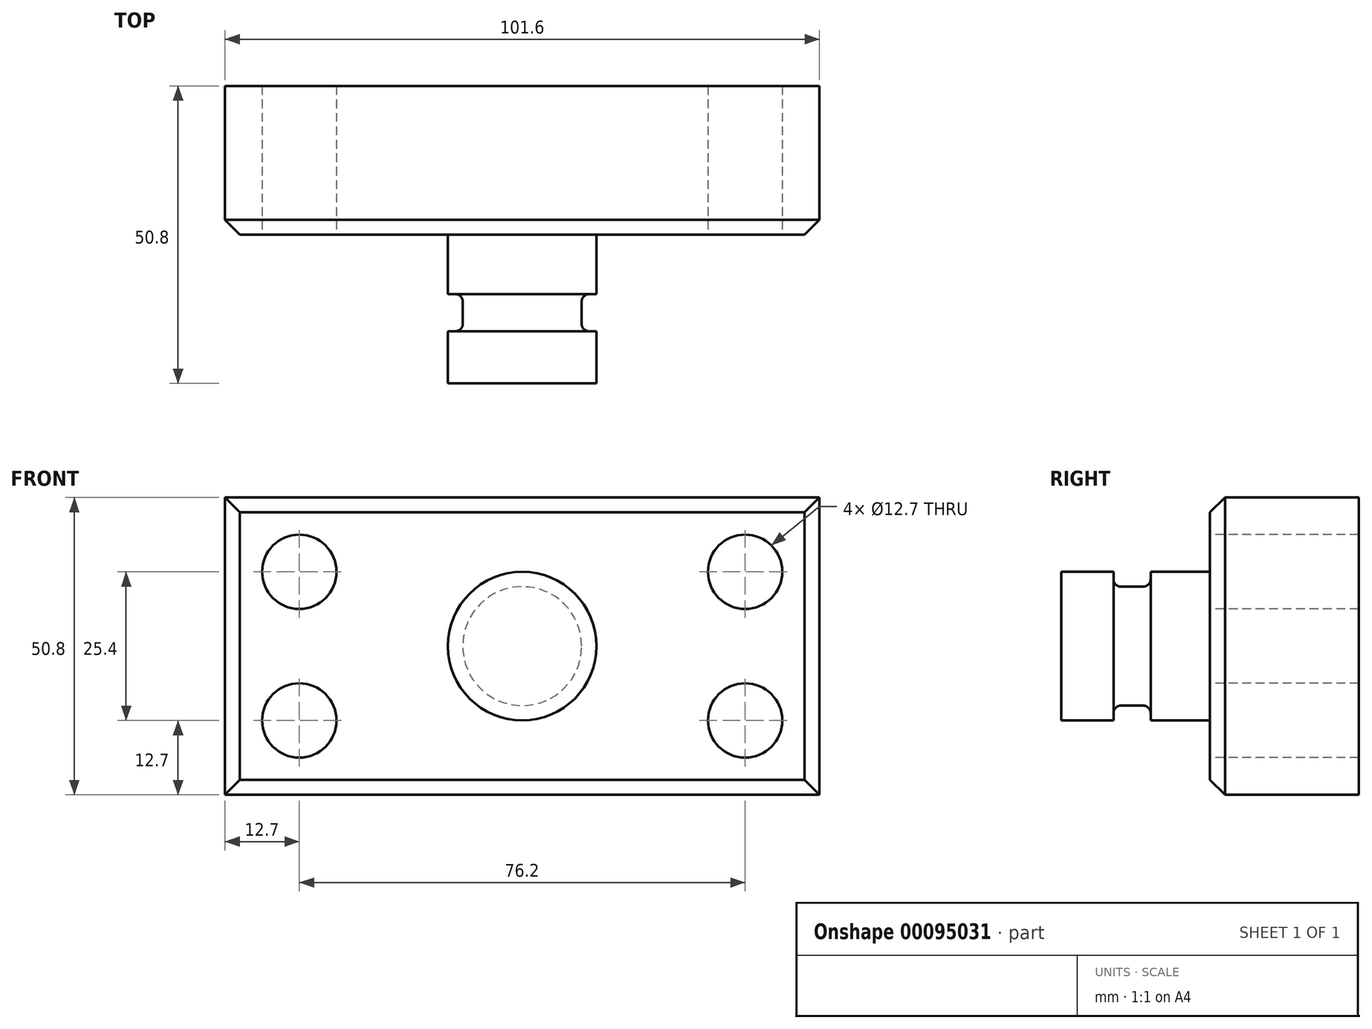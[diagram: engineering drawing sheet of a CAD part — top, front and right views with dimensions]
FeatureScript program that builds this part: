
annotation { "Feature Type Name" : "Feature", "Feature Type Description" : "" }
export const myFeature = defineFeature(function(context is Context, id is Id, definition is map)
    precondition{}
    {
        {
            var Q0;
            Q0=qCreatedBy(makeId("Front.planeOp"),FACE);
            var sketch = newSketch(context, id + "F0", { "sketchPlane" : qUnion([Q0])});
            skLineSegment(sketch, "E0.bottom", {"start": v(-50.8, 25.4) * mm, "end": v(50.8, 25.4) * mm});
            skLineSegment(sketch, "E0.top", {"start": v(-50.8, -25.4) * mm, "end": v(50.8, -25.4) * mm});
            skLineSegment(sketch, "E0.left", {"start": v(-50.8, 25.4) * mm, "end": v(-50.8, -25.4) * mm});
            skLineSegment(sketch, "E0.right", {"start": v(50.8, 25.4) * mm, "end": v(50.8, -25.4) * mm});
            skPoint(sketch, "E0.middle", {"position": v(0, 0) * mm});
            skSolve(sketch);
        }
        {
            var Q0;
            Q0 = qSketchRegion(id + "F0", true);
            extrude(context, id + "F1", {"entities" : qUnion([Q0]), "depth" : 25.4 * mm});
        }
        {
            var Q0;
            Q0=makeQuery(id+"F1.opExtrude","CAP_FACE",FACE,{"disambiguationData":[OSD([sQuery(id+"F0.wireOp",EDGE,"E0.bottom"),sQuery(id+"F0.wireOp",EDGE,"E0.top"),sQuery(id+"F0.wireOp",EDGE,"E0.left"),sQuery(id+"F0.wireOp",EDGE,"E0.right")])],"isStart":false});
            var sketch = newSketch(context, id + "F2", { "sketchPlane" : qUnion([Q0])});
            skCircle(sketch, "E1", {"center": v(-38.1, 12.7) * mm, "radius": 6.35 * mm});
            skCircle(sketch, "E2", {"center": v(-38.1, -12.7) * mm, "radius": 6.35 * mm});
            skCircle(sketch, "E3", {"center": v(38.1, 12.7) * mm, "radius": 6.35 * mm});
            skCircle(sketch, "E4", {"center": v(38.1, -12.7) * mm, "radius": 6.35 * mm});
            skSolve(sketch);
        }
        {
            var Q0;
            Q0 = qSketchRegion(id + "F2", true);
            extrude(context, id + "F3", {"entities" : qUnion([Q0]), "operationType" : NewBodyOperationType.REMOVE, "endBound" : BoundingType.THROUGH_ALL, "oppositeDirection" : true, "depth" : 25.4 * mm});
        }
        {
            var Q0;
            Q0=qCreatedBy(makeId("Top.planeOp"),FACE);
            var sketch = newSketch(context, id + "F4", { "sketchPlane" : qUnion([Q0])});
            skLineSegment(sketch, "E5.bottom", {"start": v(0, -25.4) * mm, "end": v(-12.7, -25.4) * mm});
            skLineSegment(sketch, "E5.top", {"start": v(0, -50.8) * mm, "end": v(-12.7, -50.8) * mm});
            skLineSegment(sketch, "E5.left", {"start": v(0, -25.4) * mm, "end": v(0, -50.8) * mm});
            skLineSegment(sketch, "E5.right", {"start": v(-12.7, -25.4) * mm, "end": v(-12.7, -50.8) * mm});
            skSolve(sketch);
        }
        {
            var Q0;
            Q0 = qSketchRegion(id + "F4", true);
            var Q1;
            Q1=sQuery(id+"F4.wireOp",EDGE,"E5.left");
            revolve(context, id + "F5", {"operationType" : NewBodyOperationType.ADD, "entities" : qUnion([Q0]), "axis" : qUnion([Q1]), "revolveType" : RevolveType.FULL});
        }
        {
            var Q0;
            Q0=qCreatedBy(makeId("Top.planeOp"),FACE);
            var sketch = newSketch(context, id + "F6", { "sketchPlane" : qUnion([Q0])});
            skLineSegment(sketch, "E6.bottom", {"start": v(-14.4, -41.91) * mm, "end": v(-10.16, -41.91) * mm});
            skLineSegment(sketch, "E6.top", {"start": v(-14.4, -35.56) * mm, "end": v(-10.16, -35.56) * mm});
            skLineSegment(sketch, "E6.left", {"start": v(-14.4, -41.91) * mm, "end": v(-14.4, -35.56) * mm});
            skLineSegment(sketch, "E6.right", {"start": v(-10.16, -41.91) * mm, "end": v(-10.16, -35.56) * mm});
            skLineSegment(sketch, "E7", {"start": v(0, 0) * mm, "end": v(0, -61.96) * mm, "construction": true});
            skSolve(sketch);
        }
        {
            var Q0;
            Q0 = qSketchRegion(id + "F6", true);
            var Q1;
            Q1=sQuery(id+"F6.wireOp",EDGE,"E7");
            revolve(context, id + "F7", {"operationType" : NewBodyOperationType.REMOVE, "entities" : qUnion([Q0]), "axis" : qUnion([Q1]), "revolveType" : RevolveType.FULL, "oppositeDirection" : true});
        }
        {
            var Q0;
            Q0=makeQuery(id+"F5.opRevolve","SWEPT_EDGE",EDGE,{"disambiguationData":[OSD([sQuery(id+"F4.wireOp",EDGE,"E5.bottom"),sQuery(id+"F4.wireOp",EDGE,"E5.right")])]});
            var Q1;
            Q1=makeQuery(id+"F7.boolean.opBoolean","COPY",EDGE,{"derivedFrom":makeQuery(id+"F7.opRevolve","SWEPT_EDGE",EDGE,{"disambiguationData":[OSD([sQuery(id+"F6.wireOp",EDGE,"E6.bottom"),sQuery(id+"F6.wireOp",EDGE,"E6.right")])]})});
            var Q2;
            Q2=makeQuery(id+"F7.boolean.opBoolean","COPY",EDGE,{"derivedFrom":makeQuery(id+"F7.opRevolve","SWEPT_EDGE",EDGE,{"disambiguationData":[OSD([sQuery(id+"F6.wireOp",EDGE,"E6.top"),sQuery(id+"F6.wireOp",EDGE,"E6.right")])]})});
            fillet(context, id + "F8", {"entities" : qUnion([Q0, Q1, Q2]), "radius" : 1.27 * mm, "tangentPropagation" : true, "allowEdgeOverflow" : false});
        }
        {
            var Q0;
            Q0=makeQuery(id+"F1.opExtrude","CAP_EDGE",EDGE,{"disambiguationData":[OSD([sQuery(id+"F0.wireOp",EDGE,"E0.top")])],"isStart":false});
            var Q1;
            Q1=makeQuery(id+"F1.opExtrude","CAP_EDGE",EDGE,{"disambiguationData":[OSD([sQuery(id+"F0.wireOp",EDGE,"E0.left")])],"isStart":false});
            var Q2;
            Q2=makeQuery(id+"F1.opExtrude","CAP_EDGE",EDGE,{"disambiguationData":[OSD([sQuery(id+"F0.wireOp",EDGE,"E0.bottom")])],"isStart":false});
            var Q3;
            Q3=makeQuery(id+"F1.opExtrude","CAP_EDGE",EDGE,{"disambiguationData":[OSD([sQuery(id+"F0.wireOp",EDGE,"E0.right")])],"isStart":false});
            chamfer(context, id + "F9", {"entities" : qUnion([Q0, Q1, Q2, Q3]), "width" : 2.54 * mm, "tangentPropagation" : true});
        }
    });
